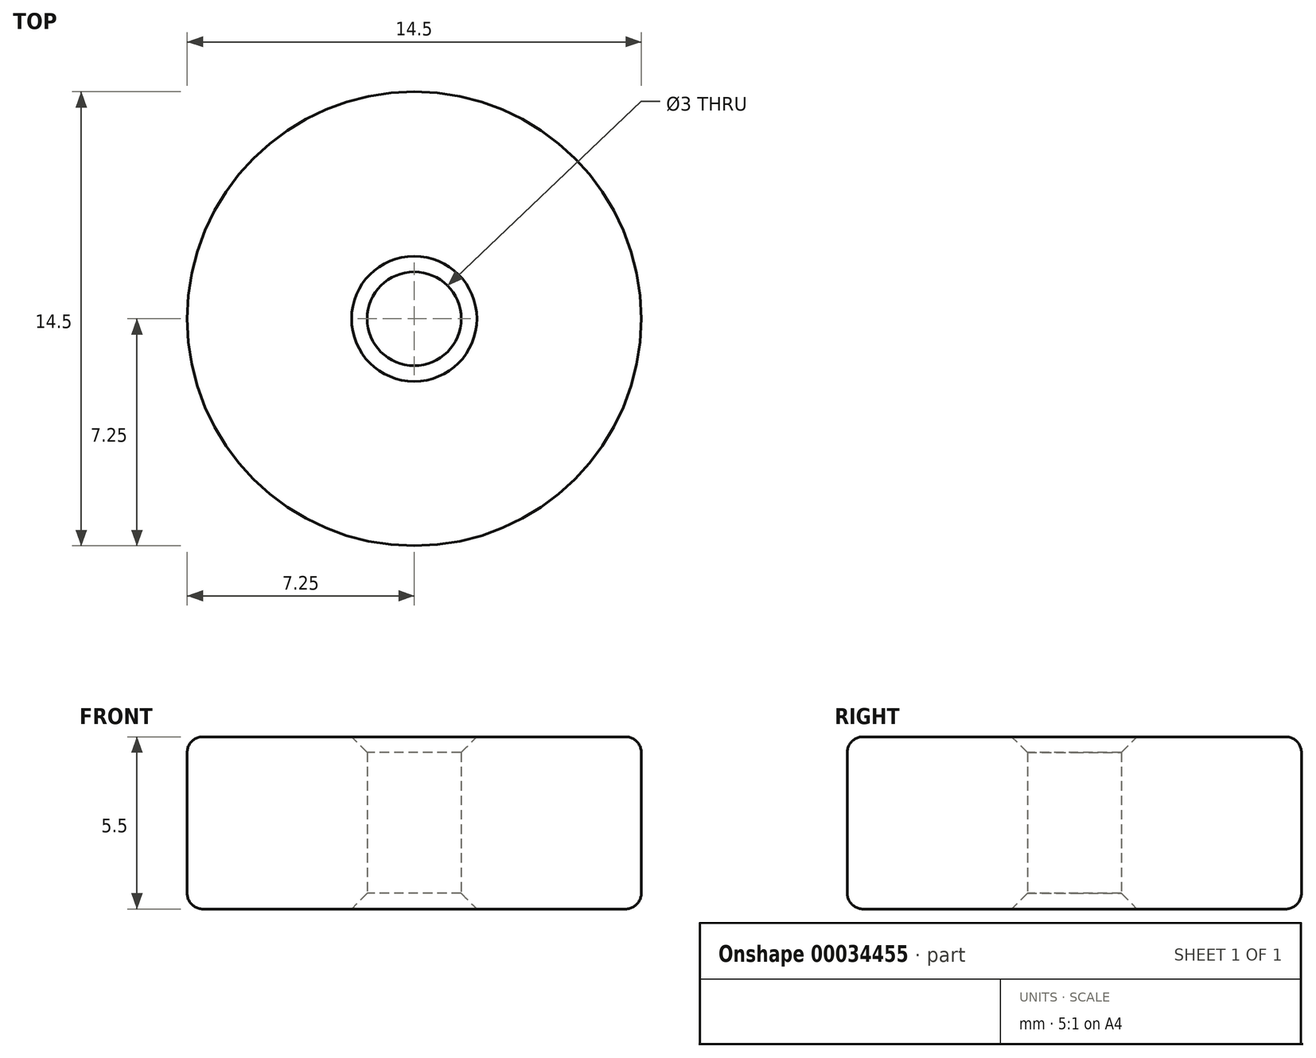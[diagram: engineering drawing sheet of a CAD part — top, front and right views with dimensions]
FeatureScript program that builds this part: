
annotation { "Feature Type Name" : "Feature", "Feature Type Description" : "" }
export const myFeature = defineFeature(function(context is Context, id is Id, definition is map)
    precondition{}
    {
        {
            var Q0;
            Q0=qCreatedBy(makeId("Top.planeOp"),FACE);
            var sketch = newSketch(context, id + "F0", { "sketchPlane" : qUnion([Q0])});
            skCircle(sketch, "E0", {"center": v(0, 0) * mm, "radius": 7.25 * mm});
            skCircle(sketch, "E1", {"center": v(0, 0) * mm, "radius": 1.5 * mm});
            skSolve(sketch);
        }
        {
            var Q0;
            Q0=makeQuery(id+"F0.imprint","IMPRINT",FACE,{"disambiguationData":[TD([[makeQuery(id+"F0.imprint","IMPRINT",EDGE,{"derivedFrom":sQuery(id+"F0.wireOp",EDGE,"E0")}),1.0]])]});
            extrude(context, id + "F1", {"entities" : qUnion([Q0]), "depth" : 5.5 * mm});
        }
        {
            var Q0;
            Q0=makeQuery(id+"F1.opExtrude","CAP_EDGE",EDGE,{"disambiguationData":[OSD([sQuery(id+"F0.wireOp",EDGE,"E1")])],"isStart":false});
            var Q1;
            Q1=makeQuery(id+"F1.opExtrude","CAP_EDGE",EDGE,{"disambiguationData":[OSD([sQuery(id+"F0.wireOp",EDGE,"E1")])],"isStart":true});
            chamfer(context, id + "F2", {"entities" : qUnion([Q0, Q1]), "width" : 0.5 * mm, "tangentPropagation" : true});
        }
        {
            var Q0;
            Q0=makeQuery(id+"F1.opExtrude","CAP_EDGE",EDGE,{"disambiguationData":[OSD([sQuery(id+"F0.wireOp",EDGE,"E0")])],"isStart":true});
            var Q1;
            Q1=makeQuery(id+"F1.opExtrude","CAP_EDGE",EDGE,{"disambiguationData":[OSD([sQuery(id+"F0.wireOp",EDGE,"E0")])],"isStart":false});
            fillet(context, id + "F3", {"entities" : qUnion([Q0, Q1]), "radius" : 0.5 * mm, "tangentPropagation" : true, "allowEdgeOverflow" : false});
        }
    });
